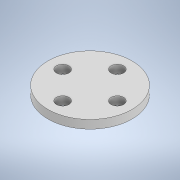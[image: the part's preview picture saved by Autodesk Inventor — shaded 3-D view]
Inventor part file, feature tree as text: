
AUTODESK INVENTOR PART (.ipt)
format: ipt  version: 2022 (Build 260153000, 153)  size: 107,520 bytes
history: native  units: mm
features: extrude x1, sketch x1
ambient origin geometry x8: Origin, YZ Plane, XZ Plane, XY Plane, X Axis, Y Axis, Z Axis, Center Point
bodies: Solid1 (feature_tree)
feature tree (2):
  extrude  "Extrusion1"  Depth=2.0mm
  sketch  "Sketch1"  dims[d0=20.0mm d1=13.0mm d2=3.0mm d3=40.0mm d5=360.0deg d7=2.0mm d8=0.0mm]
